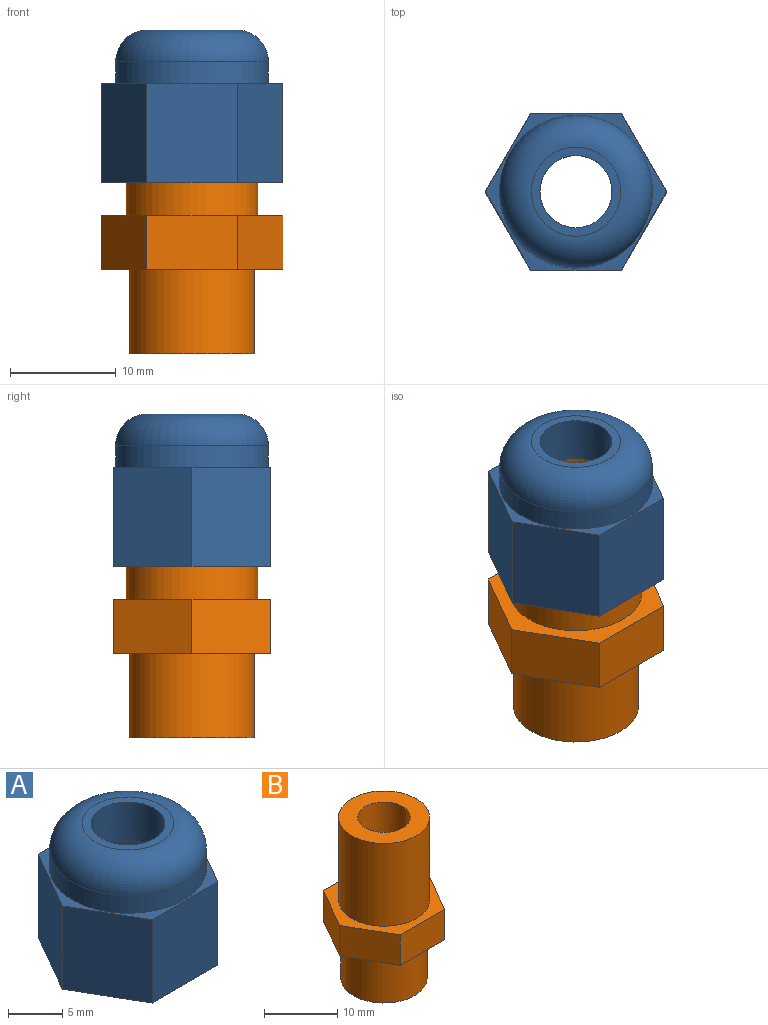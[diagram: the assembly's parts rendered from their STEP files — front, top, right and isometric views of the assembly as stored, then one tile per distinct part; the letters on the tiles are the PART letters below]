
ASSEMBLY  parts=2 mates=1
PART A: 14 faces, bbox 17.1x15.6x14.4 mm
  f0: cylinder r=3.4mm len=6.8mm, axis (0,0,-1), area 93.1mm2, adj f10,f13
  f1: plane 9.36x7.39mm, normal (0.87,0.5,0), area 79.9mm2, adj f2,f6,f7,f8
  f2: plane 9.36x8.53mm, normal (0,1,0), area 79.9mm2, adj f1,f3,f7,f8
  f3: plane 9.36x7.39mm, normal (-0.87,0.5,0), area 79.9mm2, adj f2,f4,f7,f8
  f4: plane 9.36x7.39mm, normal (-0.87,-0.5,0), area 79.9mm2, adj f3,f5,f7,f8
  f5: plane 9.36x8.53mm, normal (0,-1,0), area 79.9mm2, adj f4,f6,f7,f8
  f6: plane 9.36x7.39mm, normal (0.87,-0.5,0), area 79.9mm2, adj f1,f5,f7,f8
  f7: plane 17.07x14.78mm, normal (0,0,1), area 25.9mm2, adj f1,f2,f3,f4,f5,f6,f9
  f8: plane 17.07x14.78mm, normal (0,0,-1), area 94.1mm2, adj f1,f2,f3,f4,f5,f6,f12
  f9: cylinder r=7.21mm len=14.42mm, axis (0,0,-1), area 90.6mm2, adj f7,f11
  f10: plane 8.42x8.42mm, normal (0,0,1), area 19.4mm2, adj f0,f11
  f11: torus R=4.21mm, axis (0,0,1), area 181.2mm2, adj f9,f10
  f12: cylinder r=5.5mm len=11mm, axis (0,0,-1), area 345.6mm2, adj f8,f13
  f13: plane 11x11mm, normal (0,0,-1), area 58.7mm2, adj f0,f12
PART B: 14 faces, bbox 17.2x14.9x27 mm
  f0: plane 7.43x5.1mm, normal (0.87,0.5,0), area 43.7mm2, adj f1,f5,f6,f7
  f1: plane 8.57x5.1mm, normal (0,1,0), area 43.7mm2, adj f0,f2,f6,f7
  f2: plane 7.43x5.1mm, normal (-0.87,0.5,0), area 43.7mm2, adj f1,f3,f6,f7
  f3: plane 7.43x5.1mm, normal (-0.87,-0.5,0), area 43.7mm2, adj f2,f4,f6,f7
  f4: plane 8.57x5.1mm, normal (0,-1,0), area 43.7mm2, adj f3,f5,f6,f7
  f5: plane 7.43x5.1mm, normal (0.87,-0.5,0), area 43.7mm2, adj f0,f4,f6,f7
  f6: plane 17.15x14.85mm, normal (0,0,1), area 69.2mm2, adj f0,f1,f2,f3,f4,f5,f12
  f7: plane 17.15x14.85mm, normal (0,0,-1), area 81.6mm2, adj f0,f1,f2,f3,f4,f5,f9
  f8: cylinder r=3.6mm len=13.1mm, axis (0,0,1), area 296.7mm2, adj f10,f11
  f9: cylinder r=5.9mm len=11.8mm, axis (0,0,1), area 296.6mm2, adj f7,f10
  f10: plane 11.8x11.8mm, normal (0,0,-1), area 68.5mm2, adj f8,f9
  f11: cylinder r=3.6mm len=13.85mm, axis (0,0,-1), area 313.3mm2, adj f8,f13
  f12: cylinder r=6.22mm len=13.85mm, axis (0,0,-1), area 541.7mm2, adj f6,f13
  f13: plane 12.45x12.45mm, normal (0,0,1), area 81mm2, adj f11,f12
PLACE A t=(10.04,11.54,1.43)mm
PLACE B t=(10.04,11.54,-6.76)mm
MATE fastened B.f11 <-> A.f0  axis (0,0,-1) through (10.04,11.54,12.19)mm
